# Revit family: Faucet-Two_Handle-American_Standard-7353.841
name_source: partatom
category: Plumbing Fixtures
revit_build: Autodesk Revit 2014 (Build: 20130308_1515(x64)
units: mm (PartAtom-declared; Revit-internal decimal feet)

## types (1)
- 7353.841
    ADA Compliant = Yes
    Assembly Code = D2010900
    CW Connection = Yes
    CWFU = 1.5
    Default Elevation = 0' - 0"
    Description = Townsend Two-Handle Widespread Lavatory Faucet. Metal Speed Connect pop-up drain. Metal Lever Handles. Cast brass spout. Cast brass inlet shanks and 24" stainless steal braided flexible supply hoses with 3/8” compression connectors. 20 inch (500 mm) long flexible stainless steel drain cable is pre-assembled to faucet body
    HW Connection = Yes
    HWFU = 1.5
    Manufacturer = American Standard
    Material = Polished Chrome-American Standard-002
    Model = 7353.841
    Product Documentation Link = http://www.americanstandard-us.com
    Product Page URL = http://www.americanstandard-us.com
    Revised Date = 05/30/2016
    URL = http://www.americanstandard.ca
    Vent Connection = No
    WFU = 2
    Waste Connection = No

## geometry (parser evidence)
native form markers: Sweep x5
no freeform markers — native parametric forms only
